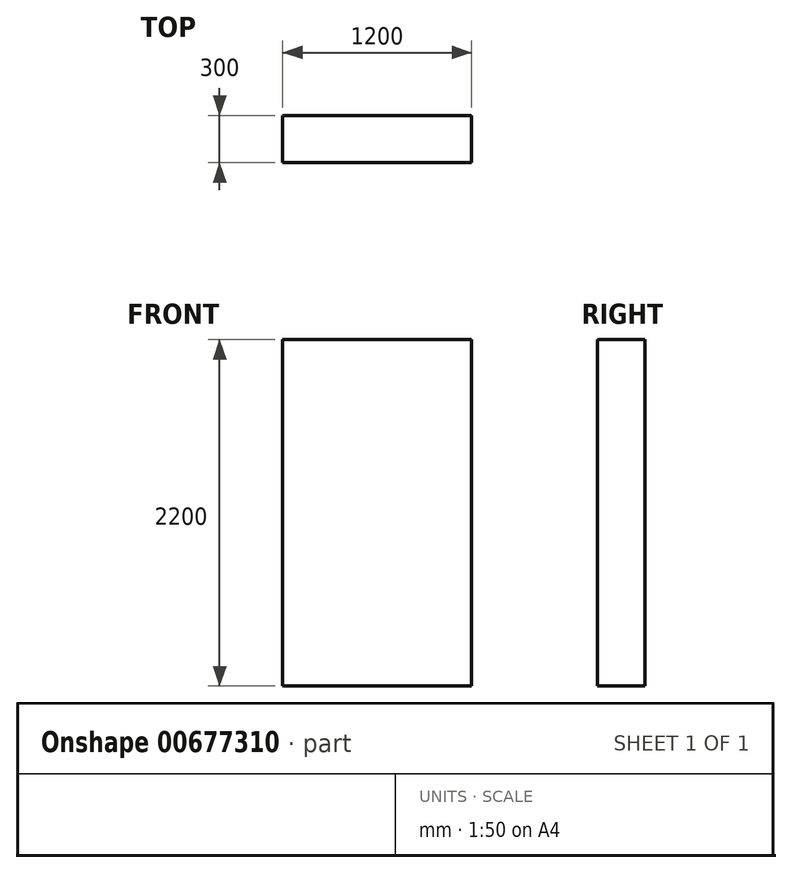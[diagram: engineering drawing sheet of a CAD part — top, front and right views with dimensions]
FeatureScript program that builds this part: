
annotation { "Feature Type Name" : "Feature", "Feature Type Description" : "" }
export const myFeature = defineFeature(function(context is Context, id is Id, definition is map)
    precondition{}
    {
        {
            var Q0;
            Q0=qCreatedBy(makeId("Front.planeOp"),FACE);
            var sketch = newSketch(context, id + "F0", { "sketchPlane" : qUnion([Q0])});
            skLineSegment(sketch, "E0.bottom", {"start": v(61.64, 0) * mm, "end": v(1261.64, 0) * mm});
            skLineSegment(sketch, "E0.top", {"start": v(61.64, 2200) * mm, "end": v(1261.64, 2200) * mm});
            skLineSegment(sketch, "E0.left", {"start": v(61.64, 0) * mm, "end": v(61.64, 2200) * mm});
            skLineSegment(sketch, "E0.right", {"start": v(1261.64, 0) * mm, "end": v(1261.64, 2200) * mm});
            skSolve(sketch);
        }
        {
            var Q0;
            Q0=makeQuery(id+"F0.imprint","IMPRINT",FACE,{"disambiguationData":[TD([[makeQuery(id+"F0.imprint","IMPRINT",EDGE,{"derivedFrom":sQuery(id+"F0.wireOp",EDGE,"E0.bottom")}),1.0]])]});
            extrude(context, id + "F1", {"entities" : qUnion([Q0]), "depth" : 300 * mm, "offsetDistance" : 25 * mm});
        }
    });
